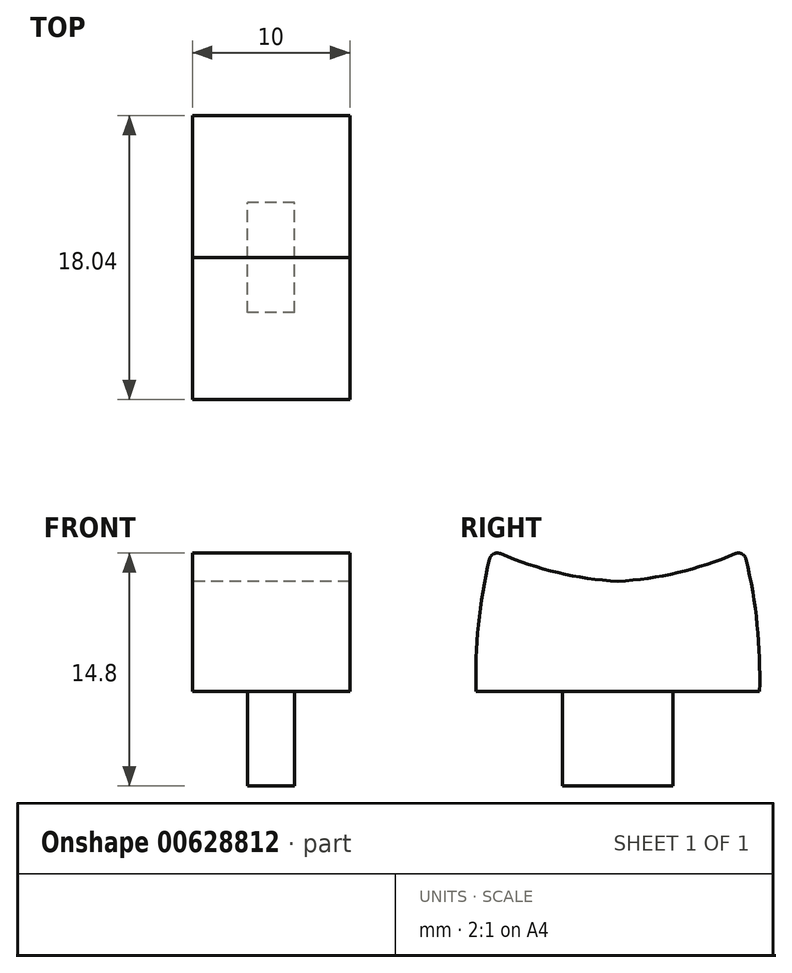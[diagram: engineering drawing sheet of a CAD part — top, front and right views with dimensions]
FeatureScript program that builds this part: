
annotation { "Feature Type Name" : "Feature", "Feature Type Description" : "" }
export const myFeature = defineFeature(function(context is Context, id is Id, definition is map)
    precondition{}
    {
        {
            var Q0;
            Q0=qCreatedBy(makeId("Right.planeOp"),FACE);
            var sketch = newSketch(context, id + "F0", { "sketchPlane" : qUnion([Q0])});
            skLineSegment(sketch, "E0", {"start": v(0, 12.85) * mm, "end": v(0, -12.15) * mm, "construction": true});
            skArc(sketch, "E1", {"start": v(-7.46, 6.36) * mm, "mid": v(-3.8, 5.15) * mm, "end": v(0, 4.6) * mm});
            skLineSegment(sketch, "E2", {"start": v(-9, -2.4) * mm, "end": v(0, -2.4) * mm});
            skArc(sketch, "E3", {"start": v(-8.14, 6.02) * mm, "mid": v(-8.85, 1.84) * mm, "end": v(-9, -2.4) * mm});
            skPoint(sketch, "E4.visualSharp", {"position": v(-8, 6.6) * mm});
            skArc(sketch, "E4.filletArc", {"start": v(-7.46, 6.36) * mm, "mid": v(-7.88, 6.35) * mm, "end": v(-8.14, 6.02) * mm});
            skArc(sketch, "E5.MirrorCS", {"start": v(7.46, 6.36) * mm, "mid": v(3.8, 5.15) * mm, "end": v(0, 4.6) * mm});
            skArc(sketch, "E6.MirrorCS", {"start": v(7.46, 6.36) * mm, "mid": v(7.88, 6.35) * mm, "end": v(8.14, 6.02) * mm});
            skLineSegment(sketch, "E7.MirrorCS", {"start": v(9, -2.4) * mm, "end": v(0, -2.4) * mm});
            skArc(sketch, "E8.MirrorCS", {"start": v(8.14, 6.02) * mm, "mid": v(8.85, 1.84) * mm, "end": v(9, -2.4) * mm});
            skSolve(sketch);
        }
        {
            var Q0;
            Q0 = qSketchRegion(id + "F0", true);
            extrude(context, id + "F1", {"entities" : qUnion([Q0]), "depth" : 10 * mm, "offsetDistance" : 25 * mm, "symmetric" : true});
        }
        {
            var Q0;
            Q0=makeQuery(id+"F1.opExtrude","SWEPT_FACE",FACE,{"disambiguationData":[OSD([sQuery(id+"F0.wireOp",EDGE,"E2"),sQuery(id+"F0.wireOp",EDGE,"E7.MirrorCS")])]});
            var sketch = newSketch(context, id + "F2", { "sketchPlane" : qUnion([Q0])});
            skLineSegment(sketch, "E9.bottom", {"start": v(1.5, 3.5) * mm, "end": v(-1.5, 3.5) * mm});
            skLineSegment(sketch, "E9.top", {"start": v(1.5, -3.5) * mm, "end": v(-1.5, -3.5) * mm});
            skLineSegment(sketch, "E9.left", {"start": v(1.5, 3.5) * mm, "end": v(1.5, -3.5) * mm});
            skLineSegment(sketch, "E9.right", {"start": v(-1.5, 3.5) * mm, "end": v(-1.5, -3.5) * mm});
            skPoint(sketch, "E9.middle", {"position": v(0, 0) * mm});
            skSolve(sketch);
        }
        {
            var Q0;
            Q0 = qSketchRegion(id + "F2", true);
            extrude(context, id + "F3", {"entities" : qUnion([Q0]), "operationType" : NewBodyOperationType.ADD, "depth" : 6 * mm, "offsetDistance" : 25 * mm});
        }
    });
